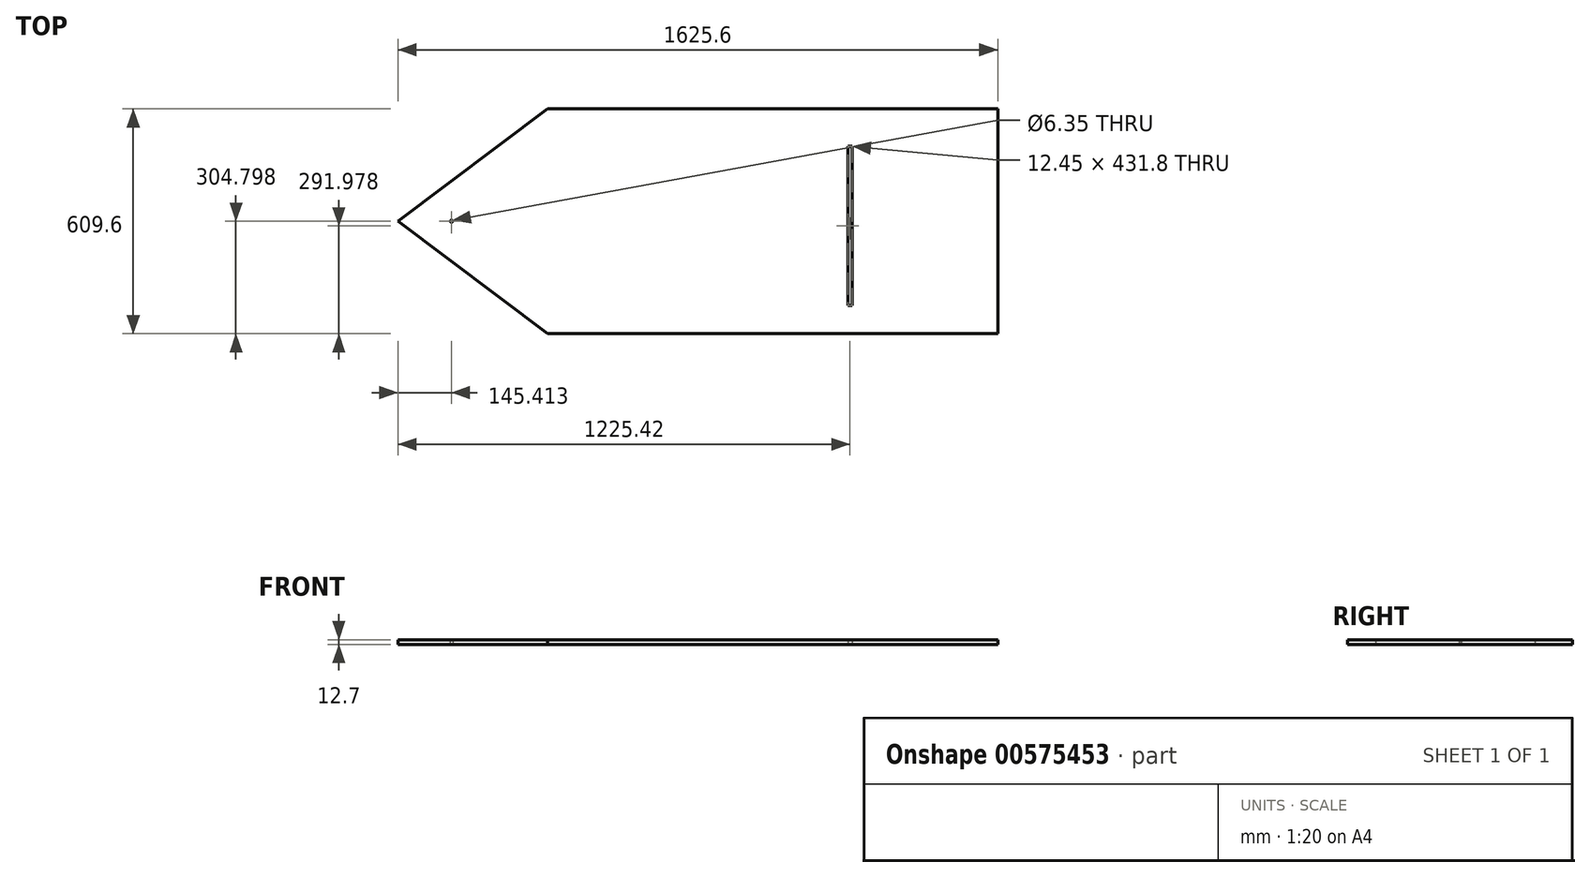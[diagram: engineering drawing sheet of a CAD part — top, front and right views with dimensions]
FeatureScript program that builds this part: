
annotation { "Feature Type Name" : "Feature", "Feature Type Description" : "" }
export const myFeature = defineFeature(function(context is Context, id is Id, definition is map)
    precondition{}
    {
        {
            var Q0;
            Q0=qCreatedBy(makeId("Top.planeOp"),FACE);
            var sketch = newSketch(context, id + "F0", { "sketchPlane" : qUnion([Q0])});
            skLineSegment(sketch, "E0.bottom", {"start": v(-616.22, 205.19) * mm, "end": v(602.98, 205.19) * mm});
            skLineSegment(sketch, "E0.top", {"start": v(-616.22, -404.41) * mm, "end": v(602.98, -404.41) * mm});
            skLineSegment(sketch, "E0.right", {"start": v(602.98, 205.19) * mm, "end": v(602.98, -404.41) * mm});
            skLineSegment(sketch, "E1", {"start": v(-616.22, 205.19) * mm, "end": v(-1022.62, -99.61) * mm});
            skPoint(sketch, "E1.endSnap0", {"position": v(-600.52, -99.61) * mm});
            skLineSegment(sketch, "E2", {"start": v(-1022.62, -99.61) * mm, "end": v(-616.22, -404.41) * mm});
            skLineSegment(sketch, "E3.bottom", {"start": v(196.58, -328.33) * mm, "end": v(209.02, -328.33) * mm});
            skLineSegment(sketch, "E3.top", {"start": v(196.58, 103.47) * mm, "end": v(209.02, 103.47) * mm});
            skLineSegment(sketch, "E3.left", {"start": v(196.58, -328.33) * mm, "end": v(196.58, 103.47) * mm});
            skLineSegment(sketch, "E3.right", {"start": v(209.02, -328.33) * mm, "end": v(209.02, 103.47) * mm});
            skCircle(sketch, "E4", {"center": v(-877.2, -99.61) * mm, "radius": 3.18 * mm});
            skSolve(sketch);
        }
        {
            var Q0;
            Q0 = qSketchRegion(id + "F0", true);
            extrude(context, id + "F1", {"entities" : qUnion([Q0]), "depth" : 12.7 * mm, "offsetDistance" : 25.4 * mm});
        }
    });
